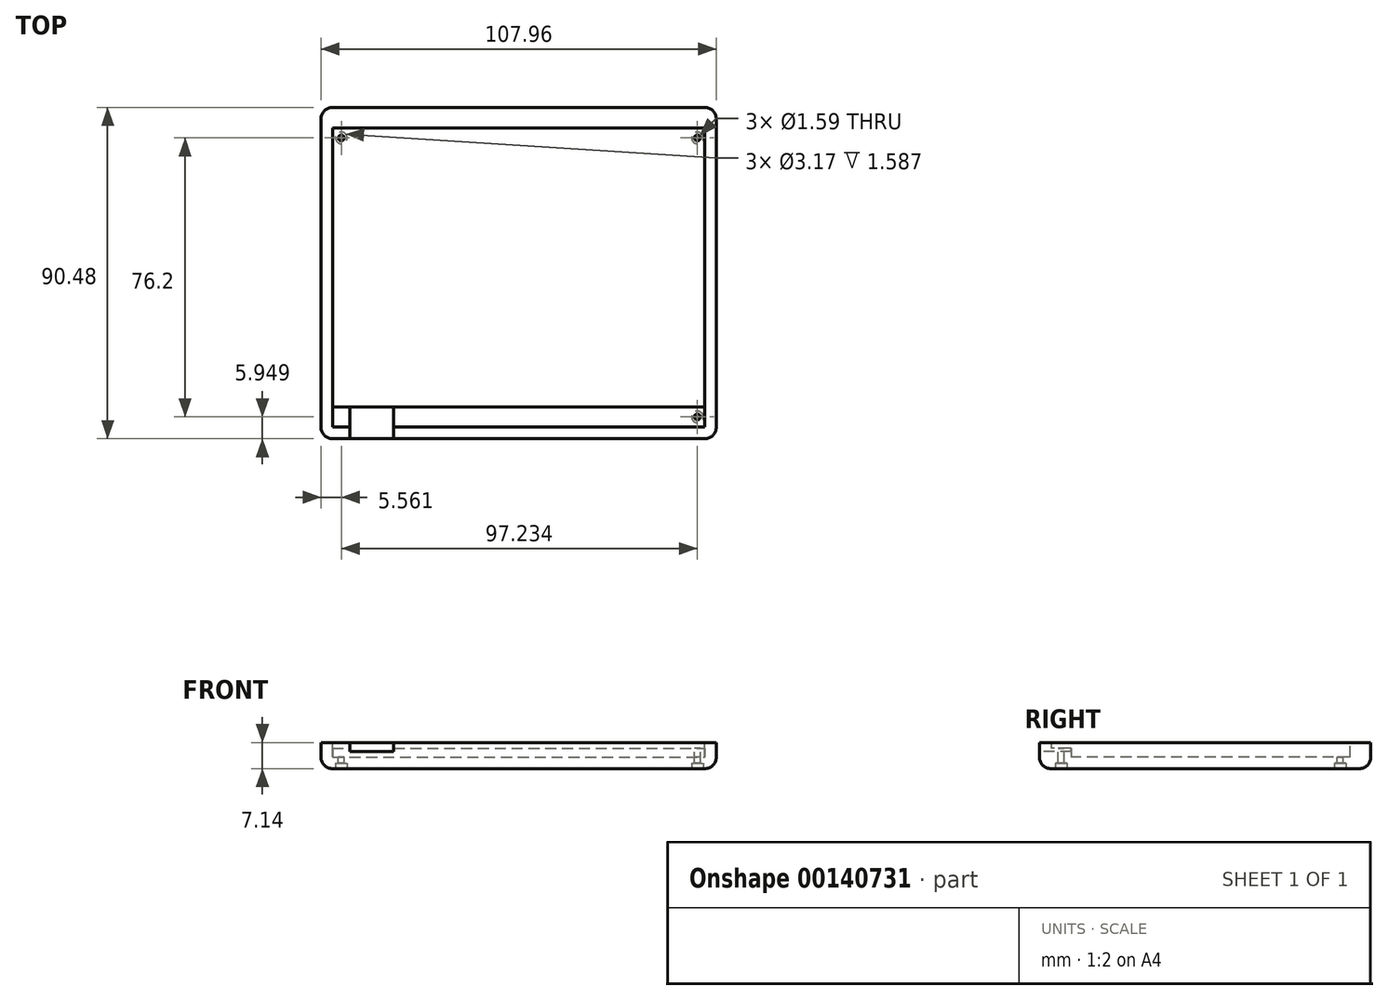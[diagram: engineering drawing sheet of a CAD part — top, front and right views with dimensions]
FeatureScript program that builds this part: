
annotation { "Feature Type Name" : "Feature", "Feature Type Description" : "" }
export const myFeature = defineFeature(function(context is Context, id is Id, definition is map)
    precondition{}
    {
        {
            var Q0;
            Q0=qCreatedBy(makeId("Top.planeOp"),FACE);
            var sketch = newSketch(context, id + "F0", { "sketchPlane" : qUnion([Q0])});
            skLineSegment(sketch, "E0.bottom", {"start": v(-53.97, -45.24) * mm, "end": v(53.98, -45.24) * mm});
            skLineSegment(sketch, "E0.top", {"start": v(-53.98, 45.24) * mm, "end": v(53.97, 45.24) * mm});
            skLineSegment(sketch, "E0.left", {"start": v(-53.98, -45.24) * mm, "end": v(-53.98, 45.24) * mm});
            skLineSegment(sketch, "E0.right", {"start": v(53.98, -45.24) * mm, "end": v(53.97, 45.24) * mm});
            skPoint(sketch, "E0.middle", {"position": v(0, 0) * mm});
            skSolve(sketch);
        }
        {
            var Q0;
            Q0=makeQuery(id+"F0.imprint","IMPRINT",FACE,{"disambiguationData":[TD([[makeQuery(id+"F0.imprint","IMPRINT",EDGE,{"derivedFrom":sQuery(id+"F0.wireOp",EDGE,"E0.bottom")}),1.0]])]});
            extrude(context, id + "F1", {"entities" : qUnion([Q0]), "depth" : 7.14 * mm});
        }
        {
            var Q0;
            Q0=makeQuery(id+"F1.opExtrude","CAP_FACE",FACE,{"disambiguationData":[OSD([sQuery(id+"F0.wireOp",EDGE,"E0.bottom"),sQuery(id+"F0.wireOp",EDGE,"E0.top"),sQuery(id+"F0.wireOp",EDGE,"E0.left"),sQuery(id+"F0.wireOp",EDGE,"E0.right")])],"isStart":false});
            var sketch = newSketch(context, id + "F2", { "sketchPlane" : qUnion([Q0])});
            skLineSegment(sketch, "E1.0.0", {"start": v(-53.98, 45.24) * mm, "end": v(-53.98, -45.24) * mm});
            skLineSegment(sketch, "E1.0.1", {"start": v(-53.97, -45.24) * mm, "end": v(53.98, -45.24) * mm});
            skLineSegment(sketch, "E1.0.2", {"start": v(53.98, -45.24) * mm, "end": v(53.97, 45.24) * mm});
            skLineSegment(sketch, "E1.0.3", {"start": v(53.97, 45.24) * mm, "end": v(-53.98, 45.24) * mm});
            skLineSegment(sketch, "E2.bottom", {"start": v(-50.8, 39.69) * mm, "end": v(50.8, 39.69) * mm});
            skLineSegment(sketch, "E2.top", {"start": v(-50.8, -42.07) * mm, "end": v(50.8, -42.07) * mm});
            skLineSegment(sketch, "E2.left", {"start": v(-50.8, 39.69) * mm, "end": v(-50.8, -42.07) * mm});
            skLineSegment(sketch, "E2.right", {"start": v(50.8, 39.69) * mm, "end": v(50.8, -42.07) * mm});
            skSolve(sketch);
        }
        {
            var Q0;
            Q0=makeQuery(id+"F2.imprint","IMPRINT",FACE,{"disambiguationData":[TD([[makeQuery(id+"F2.imprint","IMPRINT",EDGE,{"derivedFrom":sQuery(id+"F2.wireOp",EDGE,"E2.bottom")}),-1.0]])]});
            extrude(context, id + "F3", {"entities" : qUnion([Q0]), "operationType" : NewBodyOperationType.REMOVE, "oppositeDirection" : true, "depth" : 3.97 * mm});
        }
        {
            var Q0;
            Q0=makeQuery(id+"F3.boolean.opBoolean","COPY",FACE,{"derivedFrom":makeQuery(id+"F3.opExtrude","CAP_FACE",FACE,{"disambiguationData":[OSD([sQuery(id+"F2.wireOp",EDGE,"E2.bottom"),sQuery(id+"F2.wireOp",EDGE,"E2.top"),sQuery(id+"F2.wireOp",EDGE,"E2.left"),sQuery(id+"F2.wireOp",EDGE,"E2.right")])],"isStart":false})});
            var sketch = newSketch(context, id + "F4", { "sketchPlane" : qUnion([Q0])});
            skLineSegment(sketch, "E3.0.0", {"start": v(50.8, 39.69) * mm, "end": v(-50.8, 39.69) * mm});
            skLineSegment(sketch, "E3.0.1", {"start": v(-50.8, 39.69) * mm, "end": v(-50.8, -42.07) * mm});
            skLineSegment(sketch, "E3.0.2", {"start": v(-50.8, -42.07) * mm, "end": v(50.8, -42.07) * mm});
            skLineSegment(sketch, "E3.0.3", {"start": v(50.8, -42.07) * mm, "end": v(50.8, 39.69) * mm});
            skLineSegment(sketch, "E4.bottom", {"start": v(-50.8, 39.69) * mm, "end": v(50.8, 39.69) * mm});
            skLineSegment(sketch, "E4.top", {"start": v(-50.8, 34.93) * mm, "end": v(50.8, 34.93) * mm});
            skLineSegment(sketch, "E4.left", {"start": v(-50.8, 39.69) * mm, "end": v(-50.8, 34.93) * mm});
            skLineSegment(sketch, "E4.right", {"start": v(50.8, 39.69) * mm, "end": v(50.8, 34.93) * mm});
            skLineSegment(sketch, "E5.top", {"start": v(-50.8, -36.51) * mm, "end": v(50.8, -36.51) * mm});
            skLineSegment(sketch, "E5.left", {"start": v(-50.8, -42.07) * mm, "end": v(-50.8, -36.51) * mm});
            skLineSegment(sketch, "E5.right", {"start": v(50.8, -42.07) * mm, "end": v(50.8, -36.51) * mm});
            skSolve(sketch);
        }
        {
            var Q0;
            Q0=makeQuery(id+"F4.imprint","IMPRINT",FACE,{"disambiguationData":[TD([[makeQuery(id+"F4.imprint","IMPRINT",EDGE,{"derivedFrom":sQuery(id+"F4.wireOp",EDGE,"E4.bottom")}),-1.0]])]});
            var Q1;
            Q1=makeQuery(id+"F4.imprint","IMPRINT",FACE,{"disambiguationData":[TD([[makeQuery(id+"F4.imprint","IMPRINT",EDGE,{"derivedFrom":sQuery(id+"F4.wireOp",EDGE,"E3.0.2")}),1.0]])]});
            extrude(context, id + "F5", {"entities" : qUnion([Q0, Q1]), "operationType" : NewBodyOperationType.ADD, "depth" : 2.38 * mm});
        }
        {
            var Q0;
            Q0=makeQuery(id+"F1.opExtrude","SWEPT_FACE",FACE,{"disambiguationData":[OSD([sQuery(id+"F0.wireOp",EDGE,"E0.bottom")])]});
            var sketch = newSketch(context, id + "F6", { "sketchPlane" : qUnion([Q0])});
            skLineSegment(sketch, "E6.bottom", {"start": v(-46.04, 7.14) * mm, "end": v(-34.13, 7.14) * mm});
            skLineSegment(sketch, "E6.top", {"start": v(-46.04, 4.76) * mm, "end": v(-34.13, 4.76) * mm});
            skLineSegment(sketch, "E6.left", {"start": v(-46.04, 7.14) * mm, "end": v(-46.04, 4.76) * mm});
            skLineSegment(sketch, "E6.right", {"start": v(-34.13, 7.14) * mm, "end": v(-34.13, 4.76) * mm});
            skSolve(sketch);
        }
        {
            var Q0;
            Q0=makeQuery(id+"F6.imprint","IMPRINT",FACE,{"disambiguationData":[TD([[makeQuery(id+"F6.imprint","IMPRINT",EDGE,{"derivedFrom":sQuery(id+"F6.wireOp",EDGE,"E6.bottom")}),-1.0]])]});
            extrude(context, id + "F7", {"entities" : qUnion([Q0]), "operationType" : NewBodyOperationType.REMOVE, "oppositeDirection" : true, "depth" : 25.4 * mm});
        }
        {
            var Q0;
            {var subQ0=sQuery(id+"F4.wireOp",EDGE,"E5.top");Q0=makeQuery(id+"F7.boolean.opBoolean","SPLIT",FACE,{"disambiguationData":[TD([makeQuery(id+"F3.boolean.opBoolean","COPY",FACE,{"derivedFrom":makeQuery(id+"F3.opExtrude","SWEPT_FACE",FACE,{"disambiguationData":[OSD([sQuery(id+"F2.wireOp",EDGE,"E2.right")])]})})])],"derivedFrom":makeQuery(id+"F5.opExtrude","CAP_FACE",FACE,{"disambiguationData":[OSD([sQuery(id+"F4.wireOp",EDGE,"E3.0.2"),subQ0,sQuery(id+"F4.wireOp",EDGE,"E5.left"),sQuery(id+"F4.wireOp",EDGE,"E5.right")])],"isStart":false})});}
            var sketch = newSketch(context, id + "F8", { "sketchPlane" : qUnion([Q0])});
            skLineSegment(sketch, "E7.0.0", {"start": v(50.8, -36.51) * mm, "end": v(-34.13, -36.51) * mm});
            skLineSegment(sketch, "E7.0.1", {"start": v(-34.13, -36.51) * mm, "end": v(-34.13, -42.07) * mm});
            skLineSegment(sketch, "E7.0.2", {"start": v(-34.13, -42.07) * mm, "end": v(50.8, -42.07) * mm});
            skLineSegment(sketch, "E7.0.3", {"start": v(50.8, -42.07) * mm, "end": v(50.8, -36.51) * mm});
            skLineSegment(sketch, "E8.0.0", {"start": v(50.8, -42.07) * mm, "end": v(-34.13, -42.07) * mm});
            skLineSegment(sketch, "E8.0.1", {"start": v(-34.13, -42.07) * mm, "end": v(-34.13, -45.24) * mm});
            skLineSegment(sketch, "E8.0.2", {"start": v(-34.13, -45.24) * mm, "end": v(53.98, -45.24) * mm});
            skLineSegment(sketch, "E8.0.3", {"start": v(53.98, -45.24) * mm, "end": v(53.97, 45.24) * mm});
            skLineSegment(sketch, "E8.0.4", {"start": v(53.97, 45.24) * mm, "end": v(-53.98, 45.24) * mm});
            skLineSegment(sketch, "E8.0.5", {"start": v(-53.98, 45.24) * mm, "end": v(-53.98, -45.24) * mm});
            skLineSegment(sketch, "E8.0.6", {"start": v(-53.97, -45.24) * mm, "end": v(-46.04, -45.24) * mm});
            skLineSegment(sketch, "E8.0.7", {"start": v(-46.04, -45.24) * mm, "end": v(-46.04, -42.07) * mm});
            skLineSegment(sketch, "E8.0.8", {"start": v(-46.04, -42.07) * mm, "end": v(-50.8, -42.07) * mm});
            skLineSegment(sketch, "E8.0.9", {"start": v(-50.8, -42.07) * mm, "end": v(-50.8, 39.69) * mm});
            skLineSegment(sketch, "E8.0.10", {"start": v(-50.8, 39.69) * mm, "end": v(50.8, 39.69) * mm});
            skLineSegment(sketch, "E8.0.11", {"start": v(50.8, 39.69) * mm, "end": v(50.8, -42.07) * mm});
            skLineSegment(sketch, "E9.bottom", {"start": v(50.8, -42.07) * mm, "end": v(50, -42.07) * mm});
            skLineSegment(sketch, "E9.top", {"start": v(50.8, -41.28) * mm, "end": v(50, -41.28) * mm});
            skLineSegment(sketch, "E9.left", {"start": v(50.8, -42.07) * mm, "end": v(50.8, -41.28) * mm});
            skLineSegment(sketch, "E9.right", {"start": v(50, -42.07) * mm, "end": v(50, -41.28) * mm});
            skCircle(sketch, "E10", {"center": v(48.82, -39.3) * mm, "radius": 0.8 * mm});
            skLineSegment(sketch, "E11.0.0", {"start": v(-50.8, 39.69) * mm, "end": v(-50.8, 34.93) * mm});
            skLineSegment(sketch, "E11.0.1", {"start": v(-50.8, 34.93) * mm, "end": v(50.8, 34.93) * mm});
            skLineSegment(sketch, "E11.0.2", {"start": v(50.8, 34.93) * mm, "end": v(50.8, 39.69) * mm});
            skLineSegment(sketch, "E11.0.3", {"start": v(50.8, 39.69) * mm, "end": v(-50.8, 39.69) * mm});
            skLineSegment(sketch, "E12.bottom", {"start": v(50.8, 39.69) * mm, "end": v(50, 39.69) * mm});
            skLineSegment(sketch, "E12.top", {"start": v(50.8, 38.9) * mm, "end": v(50, 38.9) * mm});
            skLineSegment(sketch, "E12.left", {"start": v(50.8, 39.69) * mm, "end": v(50.8, 38.9) * mm});
            skLineSegment(sketch, "E12.right", {"start": v(50, 39.69) * mm, "end": v(50, 38.9) * mm});
            skCircle(sketch, "E13", {"center": v(48.82, 36.9) * mm, "radius": 0.8 * mm});
            skLineSegment(sketch, "E14.bottom", {"start": v(-50.8, 39.69) * mm, "end": v(-50, 39.69) * mm});
            skLineSegment(sketch, "E14.top", {"start": v(-50.8, 38.9) * mm, "end": v(-50, 38.9) * mm});
            skLineSegment(sketch, "E14.left", {"start": v(-50.8, 39.69) * mm, "end": v(-50.8, 38.9) * mm});
            skLineSegment(sketch, "E14.right", {"start": v(-50, 39.69) * mm, "end": v(-50, 38.9) * mm});
            skCircle(sketch, "E15", {"center": v(-48.42, 36.9) * mm, "radius": 0.8 * mm});
            skSolve(sketch);
        }
        {
            var Q0;
            Q0=makeQuery(id+"F8.imprint","IMPRINT",FACE,{"disambiguationData":[TD([[makeQuery(id+"F8.imprint","IMPRINT",EDGE,{"derivedFrom":sQuery(id+"F8.wireOp",EDGE,"E13")}),1.0]])]});
            var Q1;
            Q1=makeQuery(id+"F8.imprint","IMPRINT",FACE,{"disambiguationData":[TD([[makeQuery(id+"F8.imprint","IMPRINT",EDGE,{"derivedFrom":sQuery(id+"F8.wireOp",EDGE,"E10")}),1.0]])]});
            var Q2;
            Q2=makeQuery(id+"F8.imprint","IMPRINT",FACE,{"disambiguationData":[TD([[makeQuery(id+"F8.imprint","IMPRINT",EDGE,{"derivedFrom":sQuery(id+"F8.wireOp",EDGE,"E15")}),1.0]])]});
            extrude(context, id + "F9", {"entities" : qUnion([Q0, Q1, Q2]), "operationType" : NewBodyOperationType.REMOVE, "oppositeDirection" : true, "depth" : 25.4 * mm});
        }
        {
            var Q0;
            Q0=makeQuery(id+"F1.opExtrude","SWEPT_EDGE",EDGE,{"disambiguationData":[OSD([sQuery(id+"F0.wireOp",EDGE,"E0.bottom"),sQuery(id+"F0.wireOp",EDGE,"E0.right")])]});
            var Q1;
            Q1=makeQuery(id+"F1.opExtrude","SWEPT_EDGE",EDGE,{"disambiguationData":[OSD([sQuery(id+"F0.wireOp",EDGE,"E0.top"),sQuery(id+"F0.wireOp",EDGE,"E0.right")])]});
            var Q2;
            Q2=makeQuery(id+"F1.opExtrude","SWEPT_EDGE",EDGE,{"disambiguationData":[OSD([sQuery(id+"F0.wireOp",EDGE,"E0.top"),sQuery(id+"F0.wireOp",EDGE,"E0.left")])]});
            var Q3;
            Q3=makeQuery(id+"F1.opExtrude","SWEPT_EDGE",EDGE,{"disambiguationData":[OSD([sQuery(id+"F0.wireOp",EDGE,"E0.bottom"),sQuery(id+"F0.wireOp",EDGE,"E0.left")])]});
            var Q4;
            Q4=makeQuery(id+"F1.opExtrude","CAP_EDGE",EDGE,{"disambiguationData":[OSD([sQuery(id+"F0.wireOp",EDGE,"E0.bottom")])],"isStart":true});
            var Q5;
            Q5=makeQuery(id+"F1.opExtrude","CAP_EDGE",EDGE,{"disambiguationData":[OSD([sQuery(id+"F0.wireOp",EDGE,"E0.left")])],"isStart":true});
            var Q6;
            Q6=makeQuery(id+"F1.opExtrude","CAP_EDGE",EDGE,{"disambiguationData":[OSD([sQuery(id+"F0.wireOp",EDGE,"E0.top")])],"isStart":true});
            var Q7;
            Q7=makeQuery(id+"F1.opExtrude","CAP_EDGE",EDGE,{"disambiguationData":[OSD([sQuery(id+"F0.wireOp",EDGE,"E0.right")])],"isStart":true});
            fillet(context, id + "F10", {"entities" : qUnion([Q0, Q1, Q2, Q3, Q4, Q5, Q6, Q7]), "radius" : 3.17 * mm, "tangentPropagation" : true, "allowEdgeOverflow" : false});
        }
        {
            var Q0;
            Q0=makeQuery(id+"F1.opExtrude","CAP_FACE",FACE,{"disambiguationData":[OSD([sQuery(id+"F0.wireOp",EDGE,"E0.bottom"),sQuery(id+"F0.wireOp",EDGE,"E0.top"),sQuery(id+"F0.wireOp",EDGE,"E0.left"),sQuery(id+"F0.wireOp",EDGE,"E0.right")])],"isStart":true});
            var sketch = newSketch(context, id + "F11", { "sketchPlane" : qUnion([Q0])});
            skLineSegment(sketch, "E16.0.0", {"start": v(-50.8, -42.07) * mm, "end": v(50.8, -42.07) * mm});
            skLineSegment(sketch, "E16.0.1", {"start": v(50.8, -42.07) * mm, "end": v(50.8, 42.07) * mm});
            skLineSegment(sketch, "E16.0.2", {"start": v(50.8, 42.07) * mm, "end": v(-50.8, 42.07) * mm});
            skLineSegment(sketch, "E16.0.3", {"start": v(-50.8, 42.07) * mm, "end": v(-50.8, -42.07) * mm});
            skCircle(sketch, "E17", {"center": v(48.82, 39.3) * mm, "radius": 1.59 * mm});
            skCircle(sketch, "E18", {"center": v(48.82, -36.9) * mm, "radius": 1.59 * mm});
            skCircle(sketch, "E19", {"center": v(-48.42, -36.9) * mm, "radius": 1.59 * mm});
            skSolve(sketch);
        }
        {
            var Q0;
            Q0=makeQuery(id+"F11.imprint","IMPRINT",FACE,{"disambiguationData":[TD([[makeQuery(id+"F11.imprint","IMPRINT",EDGE,{"derivedFrom":sQuery(id+"F11.wireOp",EDGE,"E19")}),1.0]])]});
            var Q1;
            Q1=makeQuery(id+"F11.imprint","IMPRINT",FACE,{"disambiguationData":[TD([[makeQuery(id+"F11.imprint","IMPRINT",EDGE,{"derivedFrom":sQuery(id+"F11.wireOp",EDGE,"E18")}),1.0]])]});
            var Q2;
            Q2=makeQuery(id+"F11.imprint","IMPRINT",FACE,{"disambiguationData":[TD([[makeQuery(id+"F11.imprint","IMPRINT",EDGE,{"derivedFrom":sQuery(id+"F11.wireOp",EDGE,"E17")}),1.0]])]});
            extrude(context, id + "F12", {"entities" : qUnion([Q0, Q1, Q2]), "operationType" : NewBodyOperationType.REMOVE, "oppositeDirection" : true, "depth" : 1.59 * mm});
        }
    });
